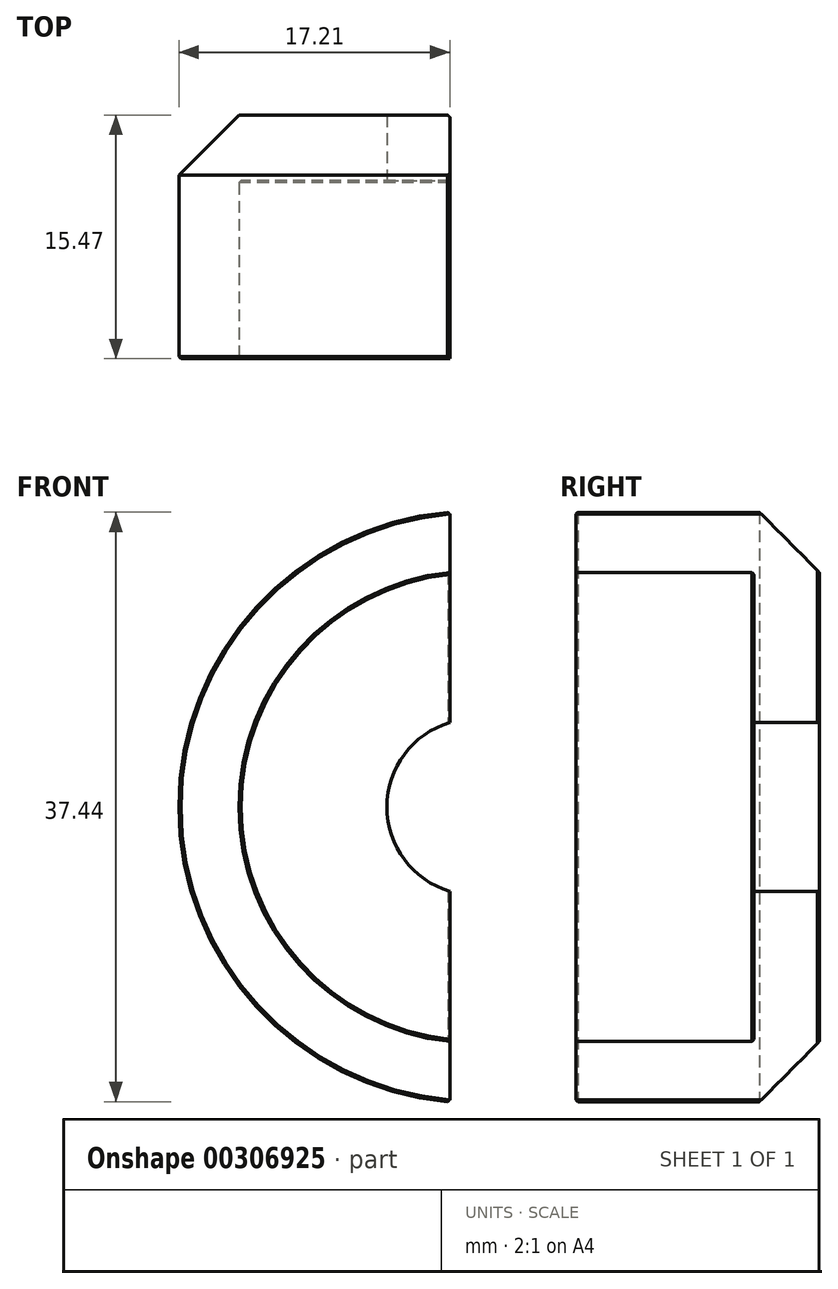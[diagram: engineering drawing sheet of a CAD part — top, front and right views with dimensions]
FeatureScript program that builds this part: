
annotation { "Feature Type Name" : "Feature", "Feature Type Description" : "" }
export const myFeature = defineFeature(function(context is Context, id is Id, definition is map)
    precondition{}
    {
        {
            var Q0;
            Q0=qCreatedBy(makeId("Front.planeOp"),FACE);
            var sketch = newSketch(context, id + "F0", { "sketchPlane" : qUnion([Q0])});
            skCircle(sketch, "E0", {"center": v(0, 0) * mm, "radius": 18.8 * mm});
            skCircle(sketch, "E1", {"center": v(0, 0) * mm, "radius": 14.99 * mm});
            skLineSegment(sketch, "E2", {"start": v(-47.82, 0) * mm, "end": v(77.82, 0) * mm, "construction": true});
            skLineSegment(sketch, "E3", {"start": v(-18.8, 0) * mm, "end": v(-18.8, 5.53) * mm, "construction": true});
            skLineSegment(sketch, "E4", {"start": v(-14.99, 0) * mm, "end": v(-14.99, 5.47) * mm, "construction": true});
            skCircle(sketch, "E5", {"center": v(0, 0) * mm, "radius": 5.59 * mm});
            skLineSegment(sketch, "E6.bottom", {"start": v(1.59, -23.24) * mm, "end": v(-1.59, -23.24) * mm});
            skLineSegment(sketch, "E6.top", {"start": v(1.59, 23.24) * mm, "end": v(-1.59, 23.24) * mm});
            skLineSegment(sketch, "E6.left", {"start": v(1.59, -23.24) * mm, "end": v(1.59, 23.24) * mm});
            skLineSegment(sketch, "E6.right", {"start": v(-1.59, -23.24) * mm, "end": v(-1.59, 23.24) * mm});
            skSolve(sketch);
        }
        {
            var Q0;
            {var subQ0=sQuery(id+"F0.wireOp",EDGE,"E6.right");var subQ1=sQuery(id+"F0.wireOp",EDGE,"E0");var subQ2=makeQuery(id+"F0.imprint","INTERSECT",VERTEX,{"disambiguationData":[OD(0.0)],"derivedFrom":[subQ1,subQ0]});Q0=makeQuery(id+"F0.imprint","IMPRINT",FACE,{"disambiguationData":[TD([[makeQuery(id+"F0.imprint","IMPRINT",EDGE,{"disambiguationData":[TD([[subQ2,-1.0]])],"derivedFrom":subQ1}),1.0]])]});}
            var Q1;
            {var subQ0=sQuery(id+"F0.wireOp",EDGE,"E6.right");var subQ1=sQuery(id+"F0.wireOp",EDGE,"E1");var subQ2=makeQuery(id+"F0.imprint","INTERSECT",VERTEX,{"disambiguationData":[OD(0.0)],"derivedFrom":[subQ1,subQ0]});Q1=makeQuery(id+"F0.imprint","IMPRINT",FACE,{"disambiguationData":[TD([[makeQuery(id+"F0.imprint","IMPRINT",EDGE,{"disambiguationData":[TD([[subQ2,-1.0]])],"derivedFrom":subQ1}),1.0]])]});}
            extrude(context, id + "F1", {"entities" : qUnion([Q0, Q1]), "oppositeDirection" : true, "depth" : 15.47 * mm});
        }
        {
            var Q0;
            {var subQ0=sQuery(id+"F0.wireOp",EDGE,"E6.right");var subQ1=sQuery(id+"F0.wireOp",EDGE,"E1");var subQ2=makeQuery(id+"F0.imprint","INTERSECT",VERTEX,{"disambiguationData":[OD(0.0)],"derivedFrom":[subQ1,subQ0]});Q0=makeQuery(id+"F0.imprint","IMPRINT",FACE,{"disambiguationData":[TD([[makeQuery(id+"F0.imprint","IMPRINT",EDGE,{"disambiguationData":[TD([[subQ2,-1.0]])],"derivedFrom":subQ1}),1.0]])]});}
            extrude(context, id + "F2", {"entities" : qUnion([Q0]), "operationType" : NewBodyOperationType.REMOVE, "oppositeDirection" : true, "depth" : 11.3 * mm});
        }
        {
            var Q0;
            Q0=makeQuery(id+"F1.opExtrude","CAP_EDGE",EDGE,{"disambiguationData":[OSD([sQuery(id+"F0.wireOp",EDGE,"E0")])],"isStart":false});
            chamfer(context, id + "F3", {"entities" : qUnion([Q0]), "width" : 3.8 * mm, "tangentPropagation" : true});
        }
        {
            var Q0;
            Q0=makeQuery(id+"F1.opExtrude","CAP_EDGE",EDGE,{"disambiguationData":[OSD([sQuery(id+"F0.wireOp",EDGE,"E0")])],"isStart":true});
            var Q1;
            Q1=makeQuery(id+"F2.boolean.opBoolean","COPY",EDGE,{"derivedFrom":makeQuery(id+"F2.opExtrude","CAP_EDGE",EDGE,{"disambiguationData":[OSD([sQuery(id+"F0.wireOp",EDGE,"E1")])],"isStart":true})});
            var Q2;
            Q2=makeQuery(id+"F2.boolean.opBoolean","COPY",EDGE,{"derivedFrom":makeQuery(id+"F2.opExtrude","CAP_EDGE",EDGE,{"disambiguationData":[OSD([sQuery(id+"F0.wireOp",EDGE,"E1")])],"isStart":false})});
            var Q3;
            {var subQ0=sQuery(id+"F0.wireOp",EDGE,"E6.right");var subQ1=sQuery(id+"F0.wireOp",EDGE,"E1");Q3=makeQuery(id+"F2.boolean.opBoolean","COPY",EDGE,{"derivedFrom":makeQuery(id+"F2.opExtrude","SWEPT_EDGE",EDGE,{"disambiguationData":[OSD([subQ1,subQ0]),TDD([makeQuery(id+"F0.imprint","INTERSECT",VERTEX,{"disambiguationData":[OD(0.0)],"derivedFrom":[subQ1,subQ0]})])]})});}
            var Q4;
            {var subQ0=sQuery(id+"F0.wireOp",EDGE,"E6.right");var subQ1=sQuery(id+"F0.wireOp",EDGE,"E1");Q4=makeQuery(id+"F2.boolean.opBoolean","COPY",EDGE,{"derivedFrom":makeQuery(id+"F2.opExtrude","SWEPT_EDGE",EDGE,{"disambiguationData":[OSD([subQ1,subQ0]),TDD([makeQuery(id+"F0.imprint","INTERSECT",VERTEX,{"disambiguationData":[OD(1.0)],"derivedFrom":[subQ1,subQ0]})])]})});}
            var Q5;
            {var subQ0=sQuery(id+"F0.wireOp",EDGE,"E6.right");var subQ1=sQuery(id+"F0.wireOp",EDGE,"E0");Q5=makeQuery(id+"F1.opExtrude","SWEPT_EDGE",EDGE,{"disambiguationData":[OSD([subQ1,subQ0]),TDD([makeQuery(id+"F0.imprint","INTERSECT",VERTEX,{"disambiguationData":[OD(0.0)],"derivedFrom":[subQ1,subQ0]})])]});}
            var Q6;
            {var subQ0=sQuery(id+"F0.wireOp",EDGE,"E6.right");var subQ1=sQuery(id+"F0.wireOp",EDGE,"E0");Q6=makeQuery(id+"F1.opExtrude","SWEPT_EDGE",EDGE,{"disambiguationData":[OSD([subQ1,subQ0]),TDD([makeQuery(id+"F0.imprint","INTERSECT",VERTEX,{"disambiguationData":[OD(1.0)],"derivedFrom":[subQ1,subQ0]})])]});}
            var Q7;
            {var subQ0=sQuery(id+"F0.wireOp",EDGE,"E6.right");Q7=makeQuery(id+"F2.boolean.opBoolean","COPY",EDGE,{"derivedFrom":makeQuery(id+"F2.opExtrude","CAP_EDGE",EDGE,{"disambiguationData":[OSD([subQ0]),TDD([makeQuery(id+"F0.imprint","IMPRINT",EDGE,{"disambiguationData":[TD([[makeQuery(id+"F0.imprint","INTERSECT",VERTEX,{"disambiguationData":[OD(0.0)],"derivedFrom":[sQuery(id+"F0.wireOp",EDGE,"E1"),subQ0]}),1.0]])],"derivedFrom":subQ0})])],"isStart":false})});}
            var Q8;
            {var subQ0=sQuery(id+"F0.wireOp",EDGE,"E6.right");Q8=makeQuery(id+"F2.boolean.opBoolean","COPY",EDGE,{"derivedFrom":makeQuery(id+"F2.opExtrude","CAP_EDGE",EDGE,{"disambiguationData":[OSD([subQ0]),TDD([makeQuery(id+"F0.imprint","IMPRINT",EDGE,{"disambiguationData":[TD([[makeQuery(id+"F0.imprint","INTERSECT",VERTEX,{"disambiguationData":[OD(1.0)],"derivedFrom":[sQuery(id+"F0.wireOp",EDGE,"E1"),subQ0]}),-1.0]])],"derivedFrom":subQ0})])],"isStart":false})});}
            var Q9;
            {var subQ0=sQuery(id+"F0.wireOp",EDGE,"E6.right");var subQ1=makeQuery(id+"F0.imprint","INTERSECT",VERTEX,{"disambiguationData":[OD(0.0)],"derivedFrom":[sQuery(id+"F0.wireOp",EDGE,"E1"),subQ0]});Q9=makeQuery(id+"F1.opExtrude","CAP_EDGE",EDGE,{"disambiguationData":[OSD([subQ0]),TDD([makeQuery(id+"F0.imprint","IMPRINT",EDGE,{"disambiguationData":[TD([[subQ1,1.0]])],"derivedFrom":subQ0}),makeQuery(id+"F0.imprint","IMPRINT",EDGE,{"disambiguationData":[TD([[makeQuery(id+"F0.imprint","INTERSECT",VERTEX,{"disambiguationData":[OD(0.0)],"derivedFrom":[sQuery(id+"F0.wireOp",EDGE,"E0"),subQ0]}),1.0]])],"derivedFrom":subQ0})])],"isStart":false});}
            var Q10;
            {var subQ0=sQuery(id+"F0.wireOp",EDGE,"E6.right");var subQ1=makeQuery(id+"F0.imprint","INTERSECT",VERTEX,{"disambiguationData":[OD(1.0)],"derivedFrom":[sQuery(id+"F0.wireOp",EDGE,"E1"),subQ0]});Q10=makeQuery(id+"F1.opExtrude","CAP_EDGE",EDGE,{"disambiguationData":[OSD([subQ0]),TDD([makeQuery(id+"F0.imprint","IMPRINT",EDGE,{"disambiguationData":[TD([[makeQuery(id+"F0.imprint","INTERSECT",VERTEX,{"disambiguationData":[OD(1.0)],"derivedFrom":[sQuery(id+"F0.wireOp",EDGE,"E0"),subQ0]}),-1.0]])],"derivedFrom":subQ0}),makeQuery(id+"F0.imprint","IMPRINT",EDGE,{"disambiguationData":[TD([[subQ1,-1.0]])],"derivedFrom":subQ0})])],"isStart":false});}
            chamfer(context, id + "F4", {"entities" : qUnion([Q0, Q1, Q2, Q3, Q4, Q5, Q6, Q7, Q8, Q9, Q10]), "width" : 0.13 * mm, "tangentPropagation" : true});
        }
    });
